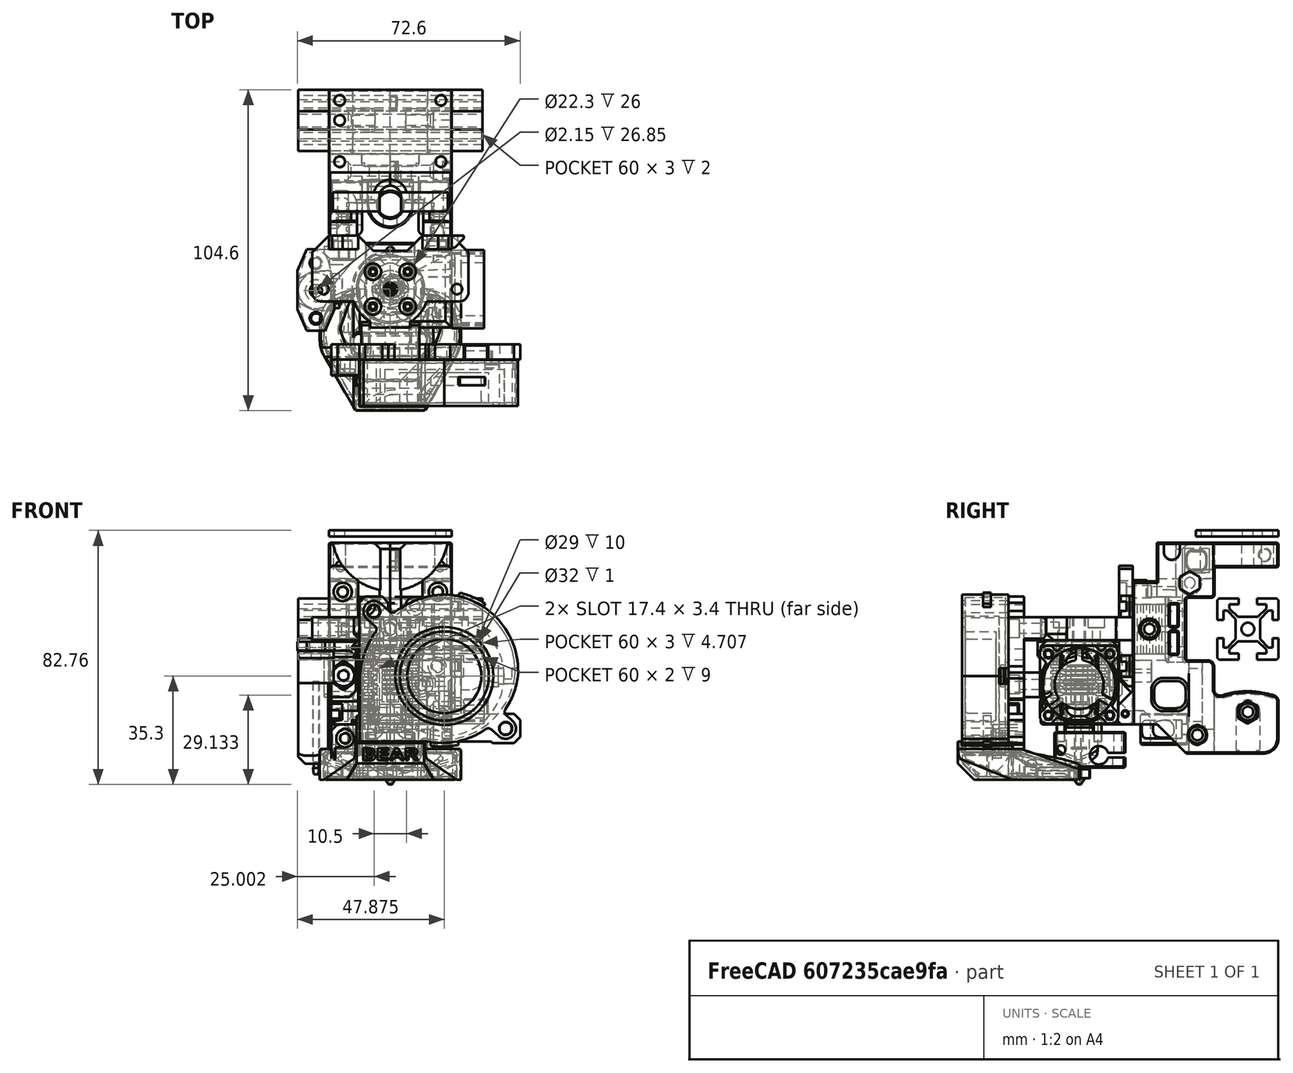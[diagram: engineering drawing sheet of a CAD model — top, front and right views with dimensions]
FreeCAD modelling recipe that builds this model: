
FCSTD DOCUMENT  (FreeCAD 0.18R16146 (Git))
Label: sherpa-mini-dragon-mount
License: Other
LicenseURL: GPL3
objects: Part::Cylinder×52, Part::Cut×38, Part::MultiFuse×35, Part::Feature×28, Part::Box×23, Part::Chamfer×22, Mesh::Feature×2, Part::Fillet×1
note: 199 computed .brp shape members not serialized (recipe doc carries the construction recipe); baked Part::Feature solids carry a one-line shape summary decoded from their .brp

FEATURE [Part::Feature] Part__Feature376001  label="Left"
  shape: bbox 22.08 x 49.92 x 69.17 mm, 332 faces (baked)
FEATURE [Part::Feature] Part__Feature377001  label="Right"
  shape: bbox 22.32 x 49.92 x 69.17 mm, 357 faces (baked)
FEATURE [Mesh::Feature] sherpa
  Placement = pos=(-4.3,-11.5,58) rot=(1,0,0;1.5708rad)
FEATURE [Part::Cylinder] Cylinder
  Angle = 360
  AttacherType = Attacher::AttachEngine3D
  Height = 20
  Placement = pos=(-1.3e-14,18.55,55.66) rot=(0.57735,-0.57735,0.57735;4.18879rad)
  Radius = 3.9
FEATURE [Part::Cylinder] Cylinder001
  Angle = 360
  AttacherType = Attacher::AttachEngine3D
  Height = 20
  Placement = pos=(-20,18.55,55.66) rot=(0.57735,-0.57735,0.57735;4.18879rad)
  Radius = 3.9
FEATURE [Part::MultiFuse] Fusion
  Shapes = -> [Cylinder001,Part__Feature376001]
FEATURE [Part::MultiFuse] Fusion004
  Shapes = -> [Part__Feature377001,Cylinder]
FEATURE [Part::Cylinder] Cylinder002
  Angle = 360
  AttacherType = Attacher::AttachEngine3D
  Height = 20
  Placement = pos=(0,14,72.1) rot=(1,0,0;1.5708rad)
  Radius = 19
FEATURE [Part::Feature] sherpa001
  Placement = pos=(0,0,2.5) rot=(0,0,1;0rad)
  shape: large baked B-rep (36 MB .brp); summary skipped
FEATURE [Part::Feature] Fusion036012039011002025018003  label="_dragon-hotend-pref"
  Placement = pos=(0,-17.5,-10) rot=(0.57735,0.57735,0.57735;2.0944rad)
  shape: bbox 22.21 x 26.11 x 45.51 mm, 390 faces, 3 solids (baked)
FEATURE [Part::Cylinder] Cylinder006
  Angle = 360
  AttacherType = Attacher::AttachEngine3D
  Height = 13
  Placement = pos=(0,0,-1) rot=(0,0,1;0rad)
  Radius = 4.15
FEATURE [Part::Cylinder] Cylinder007
  Angle = 360
  AttacherType = Attacher::AttachEngine3D
  Height = 10
  Radius = 7.5
FEATURE [Part::Cylinder] Cylinder008
  Angle = 360
  AttacherType = Attacher::AttachEngine3D
  Height = 15
  Placement = pos=(-5.25,-10,5) rot=(-1,0,0;1.5708rad)
  Radius = 2
FEATURE [Part::Cylinder] Cylinder009
  Angle = 360
  AttacherType = Attacher::AttachEngine3D
  Height = 15
  Placement = pos=(5.25,-10,5) rot=(-1,0,0;1.5708rad)
  Radius = 2
FEATURE [Part::Box] Box004  label="Cube004"
  AttacherType = Attacher::AttachEngine3D
  Height = 10
  Length = 15
  Placement = pos=(-7.5,0,0) rot=(0,0,1;0rad)
  Width = 8
FEATURE [Part::Cylinder] Cylinder010
  Angle = 360
  AttacherType = Attacher::AttachEngine3D
  Height = 7
  Placement = pos=(5.25,4,5) rot=(-1,0,0;1.5708rad)
  Radius = 1.7
FEATURE [Part::Cylinder] Cylinder011
  Angle = 360
  AttacherType = Attacher::AttachEngine3D
  Height = 7
  Placement = pos=(-5.25,4,5) rot=(-1,0,0;1.5708rad)
  Radius = 1.7
FEATURE [Part::Cylinder] Cylinder012
  Angle = 360
  AttacherType = Attacher::AttachEngine3D
  Height = 21
  Placement = pos=(-5.25,4,5) rot=(-1,0,0;1.5708rad)
  Radius = 3
FEATURE [Part::Cylinder] Cylinder013
  Angle = 360
  AttacherType = Attacher::AttachEngine3D
  Height = 21
  Placement = pos=(5.25,4,5) rot=(-1,0,0;1.5708rad)
  Radius = 3
FEATURE [Part::Box] Box005  label="Cube005"
  AttacherType = Attacher::AttachEngine3D
  Height = 6
  Length = 3
  Placement = pos=(5.25,4,2) rot=(0,0,1;0rad)
  Width = 28
FEATURE [Part::Box] Box006  label="Cube006"
  AttacherType = Attacher::AttachEngine3D
  Height = 6
  Length = 3
  Placement = pos=(-8.25,4,2) rot=(0,0,1;0rad)
  Width = 28
FEATURE [Part::Box] Box007  label="Cube007"
  AttacherType = Attacher::AttachEngine3D
  Height = 3.4
  Length = 3
  Placement = pos=(-8.25,7,3.3) rot=(0,0,1;0rad)
  Width = 3
FEATURE [Part::Box] Box008  label="Cube008"
  AttacherType = Attacher::AttachEngine3D
  Height = 3.4
  Length = 3
  Placement = pos=(5.25,7,3.3) rot=(0,0,1;0rad)
  Width = 3
FEATURE [Part::Feature] Cut001007001  label="fan-adpter"
  Placement = pos=(0,-17.5,9.5) rot=(0,0,1;0rad)
  shape: bbox 32.9 x 25.22 x 27.5 mm, 56 faces (baked)
FEATURE [Part::Feature] Part__Feature045  label="_nozzle-fan-bear"
  Placement = pos=(0.025,-17.5,-8.5) rot=(0,0,1;0rad)
  shape: bbox 46.01 x 38.99 x 18.01 mm, 128 faces (baked)
FEATURE [Part::Feature] Part__Feature041  label="_5015-fan-pref"
  Placement = pos=(-9.975,-40.6,25.3) rot=(0,0,1;1.5708rad)
  shape: bbox 52.65 x 15 x 52.12 mm, 76 faces (baked)
FEATURE [Part::Feature] Fusion036012039008  label="_2510-fan-pref"
  Placement = pos=(20.02,-17.5,22.5) rot=(0.57735,0.57735,0.57735;2.0944rad)
  shape: bbox 10.5 x 25.76 x 25.8 mm, 132 faces, 2 solids (baked)
FEATURE [Part::Feature] Fusion036012039011002025018010003001  label="fan-mount-r1-w-wire-clipper001"
  Placement = pos=(0,15,5) rot=(0,0,1;0rad)
  shape: bbox 61.58 x 12.2 x 49.65 mm, 88 faces (baked)
FEATURE [Part::Cylinder] Cylinder015
  Angle = 360
  AttacherType = Attacher::AttachEngine3D
  Height = 7.5
  Placement = pos=(0,-17.5,37) rot=(0,0,1;0rad)
  Radius = 12.5
FEATURE [Part::Box] Box009  label="Cube009"
  AttacherType = Attacher::AttachEngine3D
  Height = 7.5
  Length = 13
  Placement = pos=(-6.5,-30,37) rot=(0,0,1;0rad)
  Width = 6
FEATURE [Part::Chamfer] Chamfer001
  Base = -> Cylinder015
  Edges = 1 edges r=2: [Edge3]
FEATURE [Part::Box] Box010  label="Cube010"
  AttacherType = Attacher::AttachEngine3D
  Height = 7.5
  Length = 51
  Placement = pos=(-25.5,-21.5,37) rot=(0,0,1;0rad)
  Width = 21.5
FEATURE [Part::Box] Box011  label="Cube011"
  AttacherType = Attacher::AttachEngine3D
  Height = 47.25
  Length = 9.5
  Placement = pos=(-20,-4.5,14) rot=(0,0,1;0rad)
  Width = 4.5
FEATURE [Part::Box] Box012  label="Cube012"
  AttacherType = Attacher::AttachEngine3D
  Height = 39.25
  Length = 9.5
  Placement = pos=(10.5,-4.5,22) rot=(0,0,1;0rad)
  Width = 4.5
FEATURE [Part::Cylinder] Cylinder016
  Angle = 360
  AttacherType = Attacher::AttachEngine3D
  Height = 10
  Placement = pos=(21.75,-17.5,35) rot=(0,0,1;0rad)
  Radius = 1.7
FEATURE [Part::Cylinder] Cylinder017
  Angle = 360
  AttacherType = Attacher::AttachEngine3D
  Height = 10
  Placement = pos=(-21.75,-17.5,35) rot=(0,0,1;0rad)
  Radius = 1.7
FEATURE [Part::MultiFuse] Fusion036012039011002025018010003002
  Shapes = -> [Cylinder017,Cylinder016]
FEATURE [Part::Cut] Cut001007002
  Base = -> Box010
  Tool = -> Fusion036012039011002025018010003002
FEATURE [Part::Chamfer] Chamfer002
  Base = -> Cut001007002
  Edges = 2 edges r=5.5: [Edge3,Edge13]
FEATURE [Part::Fillet] Fillet
  Base = -> Chamfer002
  Edges = 2 edges r=3: [Edge3,Edge15]
FEATURE [Part::Chamfer] Chamfer003
  Base = -> Box009
  Edges = 2 edges r=0.4: [Edge1,Edge5]
FEATURE [Part::Box] Box013  label="Cube013"
  AttacherType = Attacher::AttachEngine3D
  Height = 10
  Length = 21
  Placement = pos=(-10.5,-5,35.5) rot=(0,0,1;0rad)
  Width = 10
FEATURE [Part::Chamfer] Chamfer007
  Base = -> Box013
  Edges = 2 edges r=5: [Edge1,Edge5]
FEATURE [Part::Cut] Cut001007004
  Base = -> Fillet
  Tool = -> Chamfer007
FEATURE [Part::Cylinder] Cylinder018
  Angle = 360
  AttacherType = Attacher::AttachEngine3D
  Height = 10
  Placement = pos=(-15.5,1.5,52.71) rot=(1,0,0;1.5708rad)
  Radius = 1.65
FEATURE [Part::Cylinder] Cylinder019
  Angle = 360
  AttacherType = Attacher::AttachEngine3D
  Height = 10
  Placement = pos=(15.5,1.2e-14,52.71) rot=(1,0,0;1.5708rad)
  Radius = 1.65
FEATURE [Part::Cylinder] Cylinder020
  Angle = 360
  AttacherType = Attacher::AttachEngine3D
  Height = 10
  Placement = pos=(15.5,1.2e-14,52.71) rot=(1,0,0;1.5708rad)
  Radius = 2.05
FEATURE [Part::Cylinder] Cylinder021
  Angle = 360
  AttacherType = Attacher::AttachEngine3D
  Height = 10
  Placement = pos=(-15.5,1.2e-14,52.71) rot=(1,0,0;1.5708rad)
  Radius = 2.05
FEATURE [Part::MultiFuse] Fusion036012039011002025018010003004003
  Placement = pos=(0,6,0) rot=(0,0,1;0rad)
  Shapes = -> [Cylinder021,Cylinder020]
FEATURE [Part::Cylinder] Cylinder022
  Angle = 360
  AttacherType = Attacher::AttachEngine3D
  Height = 10
  Placement = pos=(15.5,1.2e-14,52.71) rot=(1,0,0;1.5708rad)
  Radius = 1.7
FEATURE [Part::Cylinder] Cylinder023
  Angle = 360
  AttacherType = Attacher::AttachEngine3D
  Height = 10
  Placement = pos=(-15.5,1.2e-14,52.71) rot=(1,0,0;1.5708rad)
  Radius = 1.7
FEATURE [Part::MultiFuse] Fusion036012039011002025018010003004004
  Placement = pos=(0,14.2,0) rot=(0,0,1;0rad)
  Shapes = -> [Cylinder023,Cylinder022]
FEATURE [Part::MultiFuse] Fusion036012039011002025018010003004005
  Shapes = -> [Fusion036012039011002025018010003004004,Fusion036012039011002025018010003004003]
FEATURE [Part::Feature] Fusion036012039011002025018010003004005001  label="Fusion036012039011002025018010003004006"
  shape: bbox 35.1 x 18.2 x 4.1 mm, 10 faces, 2 solids (baked)
FEATURE [Part::Cylinder] Cylinder024
  Angle = 360
  AttacherType = Attacher::AttachEngine3D
  Height = 2.5
  Placement = pos=(-15.5,1.2e-14,52.71) rot=(1,0,0;1.5708rad)
  Radius = 3
FEATURE [Part::Cylinder] Cylinder025
  Angle = 360
  AttacherType = Attacher::AttachEngine3D
  Height = 2.5
  Placement = pos=(15.5,1.2e-14,52.71) rot=(1,0,0;1.5708rad)
  Radius = 3
FEATURE [Part::MultiFuse] Fusion036012039011002025018010003004005002
  Placement = pos=(0,-2,0) rot=(0,0,1;0rad)
  Shapes = -> [Cylinder024,Cylinder025]
FEATURE [Part::MultiFuse] Fusion036012039011002025018010003004005003
  Shapes = -> [Fusion036012039011002025018010003004005002,Cylinder018,Cylinder019]
FEATURE [Part::Cylinder] Cylinder027
  Angle = 360
  AttacherType = Attacher::AttachEngine3D
  Height = 2.5
  Placement = pos=(15.25,-5,28.5) rot=(-1,0,0;1.5708rad)
  Radius = 3
FEATURE [Part::Cylinder] Cylinder028
  Angle = 360
  AttacherType = Attacher::AttachEngine3D
  Height = 10
  Placement = pos=(15.25,-4,28.5) rot=(-1,0,0;1.5708rad)
  Radius = 2.05
FEATURE [Part::Cylinder] Cylinder029
  Angle = 360
  AttacherType = Attacher::AttachEngine3D
  Height = 10
  Placement = pos=(-15.25,-4,25.5) rot=(-1,0,0;1.5708rad)
  Radius = 2.05
FEATURE [Part::Cylinder] Cylinder030
  Angle = 360
  AttacherType = Attacher::AttachEngine3D
  Height = 10
  Placement = pos=(0,-24,40.75) rot=(1,0,0;1.5708rad)
  Radius = 2.05
FEATURE [Part::Cylinder] Cylinder031
  Angle = 360
  AttacherType = Attacher::AttachEngine3D
  Height = 10
  Placement = pos=(0,-28,40.75) rot=(1,0,0;1.5708rad)
  Radius = 1.65
FEATURE [Part::Cut] Cut001007009  label="layer-fan-mount"
  Base = -> Fusion036012039011002025018010003001
  Tool = -> Cylinder031
FEATURE [Part::Cylinder] Cylinder032
  Angle = 360
  AttacherType = Attacher::AttachEngine3D
  Height = 10
  Placement = pos=(0,-17.5,35) rot=(0,0,1;0rad)
  Radius = 2.1
FEATURE [Part::Box] Box014  label="Cube014"
  AttacherType = Attacher::AttachEngine3D
  Height = 10.5
  Length = 42
  Placement = pos=(-21,-22,-1) rot=(0,0,1;0rad)
  Width = 20
FEATURE [Part::Chamfer] Chamfer008
  Base = -> Box014
  Edges = 1 edges r=9.5: [Edge12]
  Placement = pos=(0,19.5,0) rot=(0,0,1;0rad)
FEATURE [Part::Feature] Fusion015  label="_bltouch-pref"
  Placement = pos=(-24.2,-18,33.45) rot=(0,0,1;1.5708rad)
  shape: bbox 16.68 x 26.66 x 40.15 mm, 80 faces (baked)
FEATURE [Part::Cylinder] Cylinder034
  Angle = 360
  AttacherType = Attacher::AttachEngine3D
  Height = 11
  Placement = pos=(16.3,11,9.41) rot=(1,0,0;1.5708rad)
  Radius = 3
FEATURE [Part::Feature] Chamfer008001  label="Chamfer009"
  Placement = pos=(0,19.5,0) rot=(0,0,1;0rad)
  shape: bbox 42 x 20 x 10.5 mm, 7 faces (baked)
FEATURE [Part::Feature] Fusion034001  label="probe-mount-base001"
  Placement = pos=(1.75,14.5,5) rot=(0,0,1;0rad)
  shape: bbox 19 x 27.5 x 18 mm, 47 faces (baked)
FEATURE [Part::Cylinder] Cylinder035
  Angle = 360
  AttacherType = Attacher::AttachEngine3D
  Height = 10
  Placement = pos=(15.25,-5,28.5) rot=(-1,0,0;1.5708rad)
  Radius = 1.65
FEATURE [Part::Cylinder] Cylinder036
  Angle = 360
  AttacherType = Attacher::AttachEngine3D
  Height = 10
  Placement = pos=(-15.25,-5,25.5) rot=(-1,0,0;1.5708rad)
  Radius = 1.65
FEATURE [Part::MultiFuse] Fusion036012039011002025018010003004005011
  Placement = pos=(0,0.5,0) rot=(0,0,1;0rad)
  Shapes = -> [Cylinder027,Cylinder035]
FEATURE [Part::Box] Box015  label="Cube015"
  AttacherType = Attacher::AttachEngine3D
  Height = 15
  Length = 13
  Placement = pos=(-21.5,0,0) rot=(0,0,1;0rad)
  Width = 17
FEATURE [Part::Chamfer] Chamfer008006
  Base = -> Box015
  Edges = 1 edges r=10: [Edge12]
  Placement = pos=(0,-3.5,-1) rot=(0,0,1;0rad)
FEATURE [Part::Box] Box016  label="Cube016"
  AttacherType = Attacher::AttachEngine3D
  Height = 11
  Length = 4
  Placement = pos=(16,-4.85,9.5) rot=(0,0,1;0rad)
  Width = 6
FEATURE [Part::Box] Box017  label="Cube017"
  AttacherType = Attacher::AttachEngine3D
  Height = 15
  Length = 4
  Placement = pos=(10.5,-5.5,9.5) rot=(0,0,1;0rad)
  Width = 5.4
FEATURE [Part::Chamfer] Chamfer008007
  Base = -> Box017
  Edges = 1 edges r=4.9: [Edge12]
  Placement = pos=(1.35,0,0) rot=(0,0,1;0rad)
FEATURE [Part::Chamfer] Chamfer008008
  Base = -> Chamfer008007
  Edges = 1 edges r=1: [Edge14]
FEATURE [Part::Chamfer] Chamfer008009
  Base = -> Box016
  Edges = 1 edges r=4.85: [Edge10]
FEATURE [Part::Chamfer] Chamfer008010
  Base = -> Chamfer008009
  Edges = 1 edges r=1: [Edge8]
FEATURE [Part::MultiFuse] Fusion036012039011002025018010003004005012
  Shapes = -> [Cut001007001,Chamfer008008]
FEATURE [Part::Cylinder] Cylinder037
  Angle = 360
  AttacherType = Attacher::AttachEngine3D
  Height = 10
  Placement = pos=(10.5,-2.5,13) rot=(0,1,0;1.5708rad)
  Radius = 1.15
FEATURE [Part::Cylinder] Cylinder038
  Angle = 360
  AttacherType = Attacher::AttachEngine3D
  Height = 10
  Placement = pos=(10.5,-2.5,13) rot=(0,1,0;1.5708rad)
  Radius = 0.85
FEATURE [Part::Cut] Cut001007024  label="fan-adapter"
  Base = -> Fusion036012039011002025018010003004005012
  Tool = -> Cylinder038
FEATURE [Part::Cut] Cut001007025
  Base = -> Chamfer008010
  Tool = -> Cylinder037
FEATURE [Part::Box] Box019  label="Cube018"
  AttacherType = Attacher::AttachEngine3D
  Height = 15
  Length = 1.35
  Placement = pos=(-21.5,-5,18.5) rot=(0,0,1;0rad)
  Width = 1.5
FEATURE [Part::Box] Box020  label="Cube019"
  AttacherType = Attacher::AttachEngine3D
  Height = 15
  Length = 3
  Placement = pos=(-21,-4.5,18.5) rot=(0,0,1;0rad)
  Width = 2
FEATURE [Part::Cut] Cut001007027
  Base = -> Fusion034001
  Tool = -> Box020
FEATURE [Part::Box] Box021  label="Cube020"
  AttacherType = Attacher::AttachEngine3D
  Height = 15
  Length = 1
  Placement = pos=(-21.5,-6.5,18.5) rot=(0,0,1;0rad)
  Width = 2
FEATURE [Part::Chamfer] Chamfer008011
  Base = -> Box021
  Edges = 1 edges r=0.75: [Edge1]
FEATURE [Part::MultiFuse] Fusion036012039011002025018010003004005014
  Shapes = -> [Chamfer008011,Cut001007027]
FEATURE [Part::Chamfer] Chamfer008012
  Base = -> Box019
  Edges = 2 edges r=1: [Edge11,Edge12]
FEATURE [Part::MultiFuse] Fusion036012039011002025018010003004005015
  Shapes = -> [Fusion036012039011002025018010003004005014,Chamfer008012]
FEATURE [Part::Cylinder] Cylinder041
  Angle = 360
  AttacherType = Attacher::AttachEngine3D
  Height = 3.5
  Placement = pos=(-15.25,-4.5,25.5) rot=(0.57735,-0.57735,0.57735;2.0944rad)
  Radius = 4
FEATURE [Part::Cylinder] Cylinder042
  Angle = 360
  AttacherType = Attacher::AttachEngine3D
  Height = 4.5
  Placement = pos=(-15.25,-4.5,25.5) rot=(0.57735,-0.57735,0.57735;2.0944rad)
  Radius = 1.65
FEATURE [Part::Chamfer] Chamfer008013
  Base = -> Cylinder041
  Edges = 1 edges r=0.5: [Edge1]
FEATURE [Part::Cut] Cut001007028
  Base = -> Chamfer008013
  Tool = -> Cylinder042
FEATURE [Part::MultiFuse] Fusion036012039011002025018010003004005016  label="fixed-probe"
  Shapes = -> [Cut001007028,Fusion036012039011002025018010003004005015]
FEATURE [Part::Cylinder] Cylinder043
  Angle = 360
  AttacherType = Attacher::AttachEngine3D
  Height = 10
  Placement = pos=(5.65685,-11.8431,35) rot=(0,0,1;0.785398rad)
  Radius = 1.3
FEATURE [Part::Cylinder] Cylinder044
  Angle = 360
  AttacherType = Attacher::AttachEngine3D
  Height = 10
  Placement = pos=(-5.65685,-23.1569,35) rot=(0,0,1;0.785398rad)
  Radius = 1.3
FEATURE [Part::Cylinder] Cylinder045
  Angle = 360
  AttacherType = Attacher::AttachEngine3D
  Height = 10
  Placement = pos=(-5.65685,-11.8431,35) rot=(0,0,1;0.785398rad)
  Radius = 1.3
FEATURE [Part::Cylinder] Cylinder046
  Angle = 360
  AttacherType = Attacher::AttachEngine3D
  Height = 10
  Placement = pos=(5.65685,-23.1569,35) rot=(0,0,1;0.785398rad)
  Radius = 1.3
FEATURE [Part::Cylinder] Cylinder047
  Angle = 360
  AttacherType = Attacher::AttachEngine3D
  Height = 10
  Placement = pos=(5.65685,-23.1569,35) rot=(0,0,1;0.785398rad)
  Radius = 2.5
FEATURE [Part::Cylinder] Cylinder048
  Angle = 360
  AttacherType = Attacher::AttachEngine3D
  Height = 10
  Placement = pos=(-5.65685,-11.8431,35) rot=(0,0,1;0.785398rad)
  Radius = 2.5
FEATURE [Part::Cylinder] Cylinder049
  Angle = 360
  AttacherType = Attacher::AttachEngine3D
  Height = 10
  Placement = pos=(-5.65685,-23.1569,35) rot=(0,0,1;0.785398rad)
  Radius = 2.5
FEATURE [Part::Cylinder] Cylinder050
  Angle = 360
  AttacherType = Attacher::AttachEngine3D
  Height = 10
  Placement = pos=(5.65685,-11.8431,35) rot=(0,0,1;0.785398rad)
  Radius = 2.5
FEATURE [Part::MultiFuse] Fusion036012039011002025018010003004005017
  Shapes = -> [Cylinder046,Cylinder045,Cylinder044,Cylinder043,Cylinder032]
FEATURE [Part::MultiFuse] Fusion036012039011002025018010003004005018
  Placement = pos=(0,0,6) rot=(0,0,1;0rad)
  Shapes = -> [Cylinder050,Cylinder049,Cylinder048,Cylinder047]
FEATURE [Part::MultiFuse] Fusion036012039011002025018010003004005019
  Shapes = -> [Fusion036012039011002025018010003004005017,Fusion036012039011002025018010003004005018]
FEATURE [Part::Cylinder] Cylinder051
  Angle = 360
  AttacherType = Attacher::AttachEngine3D
  Height = 10
  Placement = pos=(0,-7,72.2) rot=(-1,0,0;1.5708rad)
  Radius = 19
FEATURE [Part::MultiFuse] Fusion036012039011002025018010003004005020
  Shapes = -> [Box011,Box012]
FEATURE [Part::Chamfer] Chamfer008014
  Base = -> Fusion036012039011002025018010003004005020
  Edges = 2 edges r=3: [Edge9,Edge21]
FEATURE [Part::Cut] Cut001007031
  Base = -> Chamfer008014
  Tool = -> Cylinder051
FEATURE [Part::Chamfer] Chamfer008015
  Base = -> Cut001007031
  Edges = 2 edges r=1: [Edge3,Edge36]
FEATURE [Part::Cut] Cut001007032
  Base = -> Chamfer008015
  Tool = -> Fusion036012039011002025018010003004005003
FEATURE [Part::Cut] Cut001007033
  Base = -> Cut001007032
  Tool = -> Cylinder036
FEATURE [Part::Cut] Cut001007034
  Base = -> Cut001007033
  Tool = -> Fusion036012039011002025018010003004005011
FEATURE [Part::MultiFuse] Fusion036012039011002025018010003004005021
  Shapes = -> [Cut001007034,Cut001007004,Chamfer001,Chamfer003]
FEATURE [Part::Cut] Cut001007035
  Base = -> Fusion036012039011002025018010003004005021
  Tool = -> Fusion036012039011002025018010003004005019
FEATURE [Part::Cut] Cut001007036  label="extruder-mounter"
  Base = -> Cut001007035
  Tool = -> Cylinder030
FEATURE [Part::Feature] Fusion005001  label="Fusion036012039011002025018010003004005024"
  shape: bbox 7 x 10.5 x 10 mm, 10 faces (baked)
FEATURE [Part::Cut] Cut001007043
  Base = -> Fusion004
  Tool = -> Fusion005001
FEATURE [Part::MultiFuse] Fusion036012039011002025018010003004005022005
  Placement = pos=(0,-18,0) rot=(0,0,1;0rad)
  Shapes = -> [Cylinder012,Cylinder013]
FEATURE [Part::MultiFuse] Fusion036012039011002025018010003004005022006
  Placement = pos=(0,-25,0) rot=(0,0,1;0rad)
  Shapes = -> [Box006,Box005]
FEATURE [Part::MultiFuse] Fusion036012039011002025018010003004005022009
  Placement = pos=(0,-1,0) rot=(0,0,1;0rad)
  Shapes = -> [Box008,Cylinder008,Cylinder009,Cylinder010,Cylinder011,Box007]
FEATURE [Part::MultiFuse] Fusion036012039011002025018010003004005022010
  Placement = pos=(0,-1,0) rot=(0,0,1;0rad)
  Shapes = -> [Fusion036012039011002025018010003004005022006,Fusion036012039011002025018010003004005022005]
FEATURE [Part::MultiFuse] Fusion036012039011002025018010003004005022011
  Shapes = -> [Cylinder007,Box004]
FEATURE [Part::Chamfer] Chamfer
  Base = -> Fusion036012039011002025018010003004005022011
  Edges = 10 edges r=0.4: [Edge2,Edge4,Edge5,Edge6,Edge7,Edge9,Edge10,Edge11,Edge13,Edge15]
FEATURE [Part::Cut] Cut001007049
  Base = -> Chamfer
  Tool = -> Fusion036012039011002025018010003004005022010
FEATURE [Part::Cut] Cut001007050
  Base = -> Cut001007049
  Tool = -> Fusion036012039011002025018010003004005022009
FEATURE [Part::Cut] Cut001007051
  Base = -> Cut001007050
  Tool = -> Cylinder006
FEATURE [Part::Chamfer] Chamfer008016  label="m8-probe-mount"
  Base = -> Cut001007051
  Edges = 4 edges r=0.4: [Edge69,Edge85,Edge86,Edge89]
  Placement = pos=(0,10,3) rot=(0,0,1;0rad)
FEATURE [Part::Box] Box022  label="Cube021"
  AttacherType = Attacher::AttachEngine3D
  Height = 7
  Length = 4
  Placement = pos=(20,-10,0) rot=(0,0,1;0rad)
  Width = 4
FEATURE [Part::Box] Box023  label="Cube022"
  AttacherType = Attacher::AttachEngine3D
  Height = 3
  Length = 2
  Placement = pos=(20,-4,2) rot=(0,0,1;0rad)
  Width = 4
FEATURE [Part::Box] Box024  label="Cube023"
  AttacherType = Attacher::AttachEngine3D
  Height = 7
  Length = 4
  Placement = pos=(20,-4,0) rot=(0,0,1;0rad)
  Width = 4
FEATURE [Part::Cut] Cut001007054
  Base = -> Box024
  Tool = -> Box023
FEATURE [Part::Chamfer] Chamfer008017
  Base = -> Box022
  Edges = 1 edges r=3: [Edge3]
  Placement = pos=(1,5,0) rot=(0,0,1;0rad)
FEATURE [Part::Cut] Cut001007055
  Base = -> Cut001007054
  Tool = -> Chamfer008017
FEATURE [Part::Box] Box025  label="Cube024"
  AttacherType = Attacher::AttachEngine3D
  Height = 3
  Length = 2
  Placement = pos=(22,-6,2) rot=(0,0,1;0rad)
  Width = 4
FEATURE [Part::Cut] Cut001007056
  Base = -> Cut001007055
  Placement = pos=(0,0,25) rot=(0,0,1;0rad)
  Tool = -> Box025
FEATURE [Part::Chamfer] Chamfer008018
  Base = -> Cut001007056
  Edges = 2 edges r=0.4: [Edge16,Edge29]
FEATURE [Part::Feature] Chamfer008018001  label="Chamfer008019"
  Placement = pos=(0,0,19.5) rot=(0,0,1;0rad)
  shape: bbox 4 x 4 x 7 mm, 17 faces (baked)
FEATURE [Part::MultiFuse] Fusion036012039011002025018010003004005022012
  Shapes = -> [Chamfer008018001,Chamfer008018,Cut001007036]
FEATURE [Part::Cylinder] Cylinder052
  Angle = 360
  AttacherType = Attacher::AttachEngine3D
  Height = 11
  Placement = pos=(-16.2,11,9.41) rot=(1,0,0;1.5708rad)
  Radius = 3
FEATURE [Part::Feature] Fusion036012039011002025018010027001  label="Fusion036012039011002025018010028"
  Placement = pos=(0,15,5) rot=(0,0,1;0rad)
  shape: bbox 16.71 x 16.71 x 3.5 mm, 12 faces, 4 solids (baked)
FEATURE [Part::Cut] Cut001007062
  Base = -> Fusion036012039011002025018010003004005022012
  Tool = -> Fusion036012039011002025018010027001
FEATURE [Part::Feature] Part__Feature  label="Bear_nozzle_1"
  Placement = pos=(0,-17.5,-8.5) rot=(0,0,1;3.14159rad)
  shape: bbox 46.53 x 39.99 x 21.01 mm, 254 faces (baked)
FEATURE [Mesh::Feature] BS6RHD_E3D_fan_shroud_5020mm
  Placement = pos=(0.5,-17.5,-8.5) rot=(0,0,1;3.14159rad)
FEATURE [Part::Feature] Common001  label="2020-extrusion001"
  Placement = pos=(0,27.5,30.6) rot=(0,0,1;0rad)
  shape: bbox 60 x 20 x 20 mm, 51 faces (baked)
FEATURE [Part::Cylinder] Cylinder065
  Angle = 360
  AttacherType = Attacher::AttachEngine3D
  Height = 10
  Placement = pos=(-16.5,44,60) rot=(0,0,1;0rad)
  Radius = 2
FEATURE [Part::Cylinder] Cylinder064
  Angle = 360
  AttacherType = Attacher::AttachEngine3D
  Height = 10
  Placement = pos=(16.5,44,60) rot=(0,0,1;0rad)
  Radius = 2
FEATURE [Part::Cylinder] Cylinder066
  Angle = 360
  AttacherType = Attacher::AttachEngine3D
  Height = 10
  Placement = pos=(-16.5,24,60) rot=(0,0,1;0rad)
  Radius = 2
FEATURE [Part::Cylinder] Cylinder067
  Angle = 360
  AttacherType = Attacher::AttachEngine3D
  Height = 10
  Placement = pos=(16.5,24,60) rot=(0,0,1;0rad)
  Radius = 2
FEATURE [Part::Cylinder] Cylinder071
  Angle = 360
  AttacherType = Attacher::AttachEngine3D
  Height = 10
  Placement = pos=(-16.5,37.5,60) rot=(0,0,1;0rad)
  Radius = 2
FEATURE [Part::Feature] Chamfer008016008005001  label="Chamfer008016008007"
  shape: bbox 20 x 35 x 8 mm, 13 faces (baked)
FEATURE [Part::Feature] Chamfer008016008004001  label="Chamfer008016008006"
  shape: bbox 20 x 35 x 8 mm, 13 faces (baked)
FEATURE [Part::Feature] Cut011069020011016001  label="PCB-template001"
  shape: bbox 40 x 27 x 2 mm, 11 faces (baked)
FEATURE [Part::Feature] Cylinder073001  label="Cylinder074"
  Placement = pos=(2.2,43,64.76) rot=(0,-1,0;1.5708rad)
  shape: bbox 2.2 x 4.3 x 4.3 mm, 3 faces (baked)
FEATURE [Part::Feature] Chamfer008016008005002001  label="Chamfer008016008005003"
  shape: bbox 2 x 4 x 4 mm, 4 faces (baked)
FEATURE [Part::Feature] Cut036009013017007008008021005005044017001001  label="align-cut"
  shape: bbox 2.602 x 8 x 8 mm, 15 faces (baked)
FEATURE [Part::MultiFuse] Fusion036012039011002025018010003004005022016
  Shapes = -> [Cylinder034,Cut001007043]
FEATURE [Part::Cut] Cut036009013017007008008021005005044017001002
  Base = -> Fusion036012039011002025018010003004005022016
  Tool = -> Chamfer008001
FEATURE [Part::Cut] Cut036009013017007008008021005005044017001003
  Base = -> Cut036009013017007008008021005005044017001002
  Tool = -> Cylinder028
FEATURE [Part::Cut] Cut036009013017007008008021005005044017001004
  Base = -> Cut036009013017007008008021005005044017001003
  Tool = -> Fusion036012039011002025018010003004005001
FEATURE [Part::MultiFuse] Fusion036012039011002025018010003004005022017
  Shapes = -> [Cut001007025,Cut036009013017007008008021005005044017001004]
FEATURE [Part::Feature] Fusion005002  label="wire-router"
  shape: bbox 7 x 10.5 x 10 mm, 10 faces (baked)
FEATURE [Part::Cut] Cut
  Base = -> Fusion
  Tool = -> Cylinder029
FEATURE [Part::Cut] Cut036009013017007008008021005005044017001005
  Base = -> Cut
  Tool = -> Fusion036012039011002025018010003004005
FEATURE [Part::MultiFuse] Fusion036012039011002025018010003004005022018
  Shapes = -> [Cut036009013017007008008021005005044017001005,Cylinder052]
FEATURE [Part::Cut] Cut036009013017007008008021005005044017001006
  Base = -> Fusion036012039011002025018010003004005022018
  Tool = -> Chamfer008006
FEATURE [Part::Cut] Cut036009013017007008008021005005044017001007
  Base = -> Cut036009013017007008008021005005044017001006
  Tool = -> Chamfer008
FEATURE [Part::Cylinder] Cylinder073002
  Angle = 360
  AttacherType = Attacher::AttachEngine3D
  Height = 20
  Placement = pos=(0,14,72.1) rot=(1,0,0;1.5708rad)
  Radius = 19
FEATURE [Part::Box] Box027  label="Cube026"
  AttacherType = Attacher::AttachEngine3D
  Height = 11.76
  Length = 20
  Placement = pos=(-20,7.8,57) rot=(0,0,1;0rad)
  Width = 18.8
FEATURE [Part::Box] Box028  label="Cube027"
  AttacherType = Attacher::AttachEngine3D
  Height = 11.76
  Length = 20
  Placement = pos=(0,7.8,57) rot=(0,0,1;0rad)
  Width = 18.8
FEATURE [Part::Chamfer] Chamfer008016008005002002
  Base = -> Box028
  Edges = 5 edges r=0.4: [Edge5,Edge6,Edge7,Edge10,Edge12]
FEATURE [Part::Chamfer] Chamfer008016008005002003
  Base = -> Box027
  Edges = 5 edges r=0.4: [Edge1,Edge2,Edge3,Edge10,Edge12]
FEATURE [Part::MultiFuse] Fusion036012039011002025018010003004005022019
  Shapes = -> [Chamfer008016008005002003,Cut036009013017007008008021005005044017001007]
FEATURE [Part::MultiFuse] Fusion036012039011002025018010003004005022020
  Shapes = -> [Chamfer008016008005002002,Fusion036012039011002025018010003004005022017]
FEATURE [Part::MultiFuse] Fusion036012039011002025018010003004005022021
  Shapes = -> [Fusion036012039011002025018010003004005022020,Chamfer008016008004001]
FEATURE [Part::MultiFuse] Fusion036012039011002025018010003004005022022
  Shapes = -> [Fusion036012039011002025018010003004005022019,Chamfer008016008005001]
FEATURE [Part::Feature] Fusion036012039011002025018010003004005022023  label="wire-router001"
  Placement = pos=(0,0,10) rot=(0,0,1;0rad)
  shape: bbox 7 x 10.5 x 10 mm, 10 faces (baked)
FEATURE [Part::MultiFuse] Fusion036012039011002025018010003004005022024
  Shapes = -> [Fusion036012039011002025018010003004005022023,Fusion005002]
FEATURE [Part::Feature] Fusion036012039011002025018010003004005022024001  label="Fusion036012039011002025018010003004005022025"
  shape: bbox 7 x 10.5 x 20 mm, 14 faces (baked)
FEATURE [Part::Cut] Cut036009013017007008008021005005044017001008
  Base = -> Fusion036012039011002025018010003004005022022
  Tool = -> Fusion036012039011002025018010003004005022024
FEATURE [Part::Cut] Cut036009013017007008008021005005044017001009
  Base = -> Fusion036012039011002025018010003004005022021
  Tool = -> Fusion036012039011002025018010003004005022024001
FEATURE [Part::Cut] Cut036009013017007008008021005005044017001010
  Base = -> Cut036009013017007008008021005005044017001009
  Tool = -> Cylinder002
FEATURE [Part::Cut] Cut036009013017007008008021005005044017001011
  Base = -> Cut036009013017007008008021005005044017001008
  Tool = -> Cylinder073002
FEATURE [Part::Cut] Cut036009013017007008008021005005044017001012
  Base = -> Cut036009013017007008008021005005044017001010
  Tool = -> Cut036009013017007008008021005005044017001001
FEATURE [Part::MultiFuse] Fusion036012039011002025018010003004005022024002
  Shapes = -> [Cut036009013017007008008021005005044017001011,Chamfer008016008005002001]
FEATURE [Part::Cut] Cut036009013017007008008021005005044017001013
  Base = -> Cut036009013017007008008021005005044017001012
  Tool = -> Cylinder073001
FEATURE [Part::MultiFuse] Fusion036012039011002025018010003004005022024003
  Shapes = -> [Cylinder065,Cylinder071,Cylinder066]
FEATURE [Part::Cut] Cut036009013017007008008021005005044017001014
  Base = -> Fusion036012039011002025018010003004005022024002
  Tool = -> Fusion036012039011002025018010003004005022024003
FEATURE [Part::MultiFuse] Fusion036012039011002025018010003004005022024004
  Shapes = -> [Cylinder067,Cylinder064]
FEATURE [Part::Cut] Cut036009013017007008008021005005044017001015
  Base = -> Cut036009013017007008008021005005044017001013
  Tool = -> Fusion036012039011002025018010003004005022024004
FEATURE [Part::Cylinder] Cylinder073004
  Angle = 360
  AttacherType = Attacher::AttachEngine3D
  Height = 10
  Placement = pos=(3e-15,14.7,66.76) rot=(0,0,1;1.5708rad)
  Radius = 5.5
FEATURE [Part::Chamfer] Chamfer008016008005002004
  Base = -> Cylinder073004
  Edges = 1 edges r=2: [Edge3]
  Placement = pos=(0,-2,0) rot=(0,0,1;0rad)
FEATURE [Part::Feature] Chamfer008016008005002004001  label="Chamfer008016008005002005"
  Placement = pos=(0,-2,0) rot=(0,0,1;0rad)
  shape: bbox 11 x 11 x 10 mm, 4 faces (baked)
FEATURE [Part::Cut] Cut036009013017007008008021005005044017001018
  Base = -> Cut036009013017007008008021005005044017001015
  Tool = -> Chamfer008016008005002004
FEATURE [Part::Cut] Cut036009013017007008008021005005044017001019
  Base = -> Cut036009013017007008008021005005044017001014
  Tool = -> Chamfer008016008005002004001
